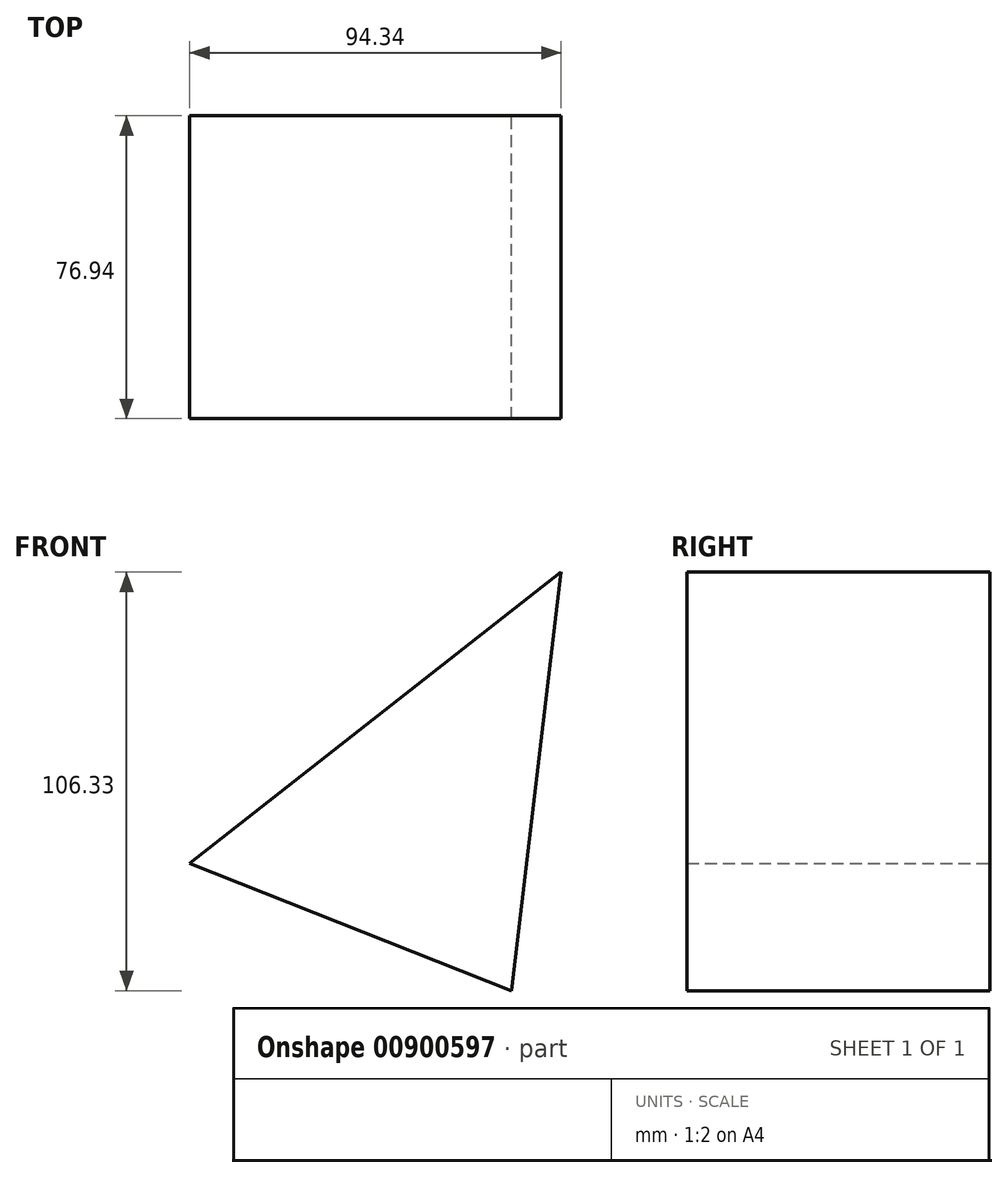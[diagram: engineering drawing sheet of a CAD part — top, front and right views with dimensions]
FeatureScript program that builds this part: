
annotation { "Feature Type Name" : "Feature", "Feature Type Description" : "" }
export const myFeature = defineFeature(function(context is Context, id is Id, definition is map)
    precondition{}
    {
        {
            var Q0;
            Q0=qCreatedBy(makeId("Front.planeOp"),FACE);
            var sketch = newSketch(context, id + "F0", { "sketchPlane" : qUnion([Q0])});
            skLineSegment(sketch, "E0", {"start": v(37.2, 57) * mm, "end": v(-57.14, -16.95) * mm});
            skLineSegment(sketch, "E1", {"start": v(-57.14, -16.95) * mm, "end": v(24.6, -49.34) * mm});
            skLineSegment(sketch, "E2", {"start": v(24.6, -49.34) * mm, "end": v(37.2, 57) * mm});
            skSolve(sketch);
        }
        {
            var Q0;
            Q0 = qSketchRegion(id + "F0", true);
            extrude(context, id + "F1", {"entities" : qUnion([Q0]), "depth" : 76.94 * mm, "offsetDistance" : 25.4 * mm});
        }
    });
